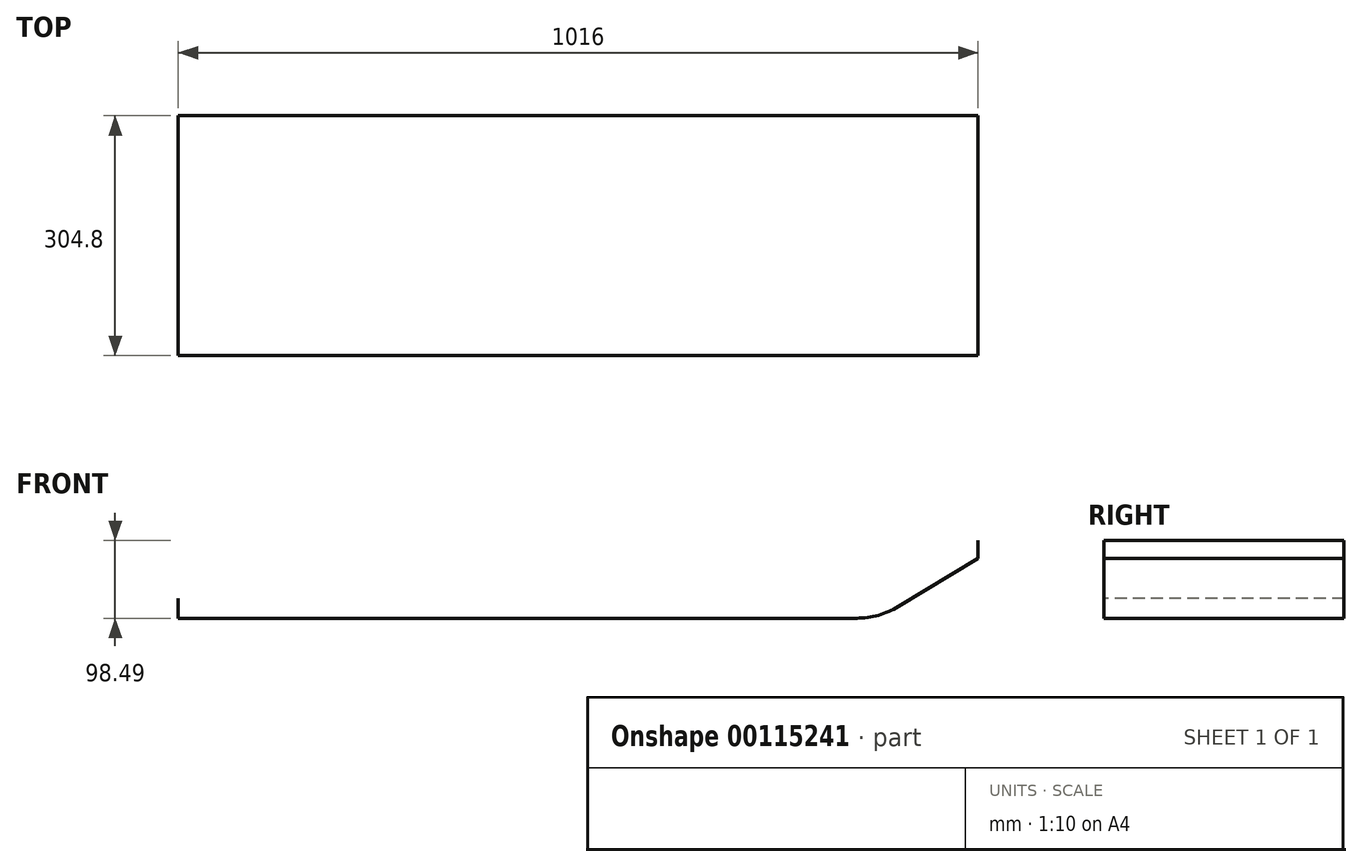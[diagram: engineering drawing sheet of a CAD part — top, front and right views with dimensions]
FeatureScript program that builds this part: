
annotation { "Feature Type Name" : "Feature", "Feature Type Description" : "" }
export const myFeature = defineFeature(function(context is Context, id is Id, definition is map)
    precondition{}
    {
        {
            var Q0;
            Q0=qCreatedBy(makeId("Front.planeOp"),FACE);
            var sketch = newSketch(context, id + "F0", { "sketchPlane" : qUnion([Q0])});
            skLineSegment(sketch, "E0", {"start": v(-537.77, 0) * mm, "end": v(324.33, 0) * mm});
            skPoint(sketch, "E1", {"position": v(478.23, 76.2) * mm});
            skPoint(sketch, "E2", {"position": v(325.83, 0) * mm});
            skLineSegment(sketch, "E3", {"start": v(377.07, 14.76) * mm, "end": v(478.23, 76.2) * mm});
            skPoint(sketch, "E4.newPointB", {"position": v(478.23, 0) * mm});
            skArc(sketch, "E4.filletArc", {"start": v(324.33, 0) * mm, "mid": v(351.71, 3.76) * mm, "end": v(377.07, 14.76) * mm});
            skLineSegment(sketch, "E5", {"start": v(478.23, 76.2) * mm, "end": v(478.23, 98.49) * mm});
            skLineSegment(sketch, "E6.0", {"start": v(367.18, 31.04) * mm, "end": v(478.23, 98.49) * mm});
            skSolve(sketch);
        }
        {
            var Q0;
            Q0=qCreatedBy(makeId("Right.planeOp"),FACE);
            var sketch = newSketch(context, id + "F6", { "sketchPlane" : qUnion([Q0])});
            skPoint(sketch, "E7", {"position": v(-152.4, 0) * mm});
            skPoint(sketch, "E8", {"position": v(152.4, 0) * mm});
            skPoint(sketch, "E9", {"position": v(-152.4, 25.4) * mm});
            skPoint(sketch, "E10", {"position": v(152.4, 25.4) * mm});
            skArc(sketch, "E11", {"start": v(-152.4, 25.4) * mm, "mid": v(0, 0) * mm, "end": v(152.4, 25.4) * mm});
            skSolve(sketch);
        }
        {
            var Q0;
            Q0=sQuery(id+"F0.wireOp",EDGE,"E3");
            var Q1;
            Q1=sQuery(id+"F0.wireOp",EDGE,"E0");
            var Q2;
            Q2=sQuery(id+"F0.wireOp",EDGE,"E4.filletArc");
            extrude(context, id + "F7", {"bodyType" : ExtendedToolBodyType.SURFACE, "surfaceEntities" : qUnion([Q0, Q1, Q2]), "depth" : 152.4 * mm, "hasSecondDirection" : true, "secondDirectionOppositeDirection" : true, "secondDirectionDepth" : 152.4 * mm});
        }
        {
            var Q0;
            Q0=makeQuery(id+"F7.opExtrude","CAP_EDGE",EDGE,{"disambiguationData":[OSD([sQuery(id+"F0.wireOp",EDGE,"E0")])],"isStart":true});
            var Q1;
            Q1=sQuery(id+"F6.wireOp",VERTEX,"E10");
            cPlane(context, id + "F1", {"entities" : qUnion([Q0, Q1]), "cplaneType" : CPlaneType.LINE_ANGLE, "offset" : 25.4 * mm, "angle" : 0 * degree, "width" : 152.4 * mm, "height" : 152.4 * mm});
        }
        {
            var Q0;
            Q0=sQuery(id+"F0.wireOp",EDGE,"E5");
            extrude(context, id + "F2", {"bodyType" : ExtendedToolBodyType.SURFACE, "surfaceEntities" : qUnion([Q0]), "oppositeDirection" : true, "depth" : 152.4 * mm, "hasSecondDirection" : true, "secondDirectionOppositeDirection" : false, "secondDirectionDepth" : 152.4 * mm});
        }
        {
            var Q0;
            Q0=makeQuery(id+"F7.opExtrude","SWEPT_FACE",FACE,{"disambiguationData":[OSD([sQuery(id+"F0.wireOp",EDGE,"E0")])]});
            var sketch = newSketch(context, id + "F8", { "sketchPlane" : qUnion([Q0])});
            skLineSegment(sketch, "E12", {"start": v(-537.77, -152.4) * mm, "end": v(-537.77, 152.4) * mm});
            skSolve(sketch);
        }
        {
            var Q0;
            Q0=sQuery(id+"F8.wireOp",EDGE,"E12");
            extrude(context, id + "F3", {"bodyType" : ExtendedToolBodyType.SURFACE, "surfaceEntities" : qUnion([Q0]), "oppositeDirection" : true, "depth" : 25.4 * mm});
        }
    });
